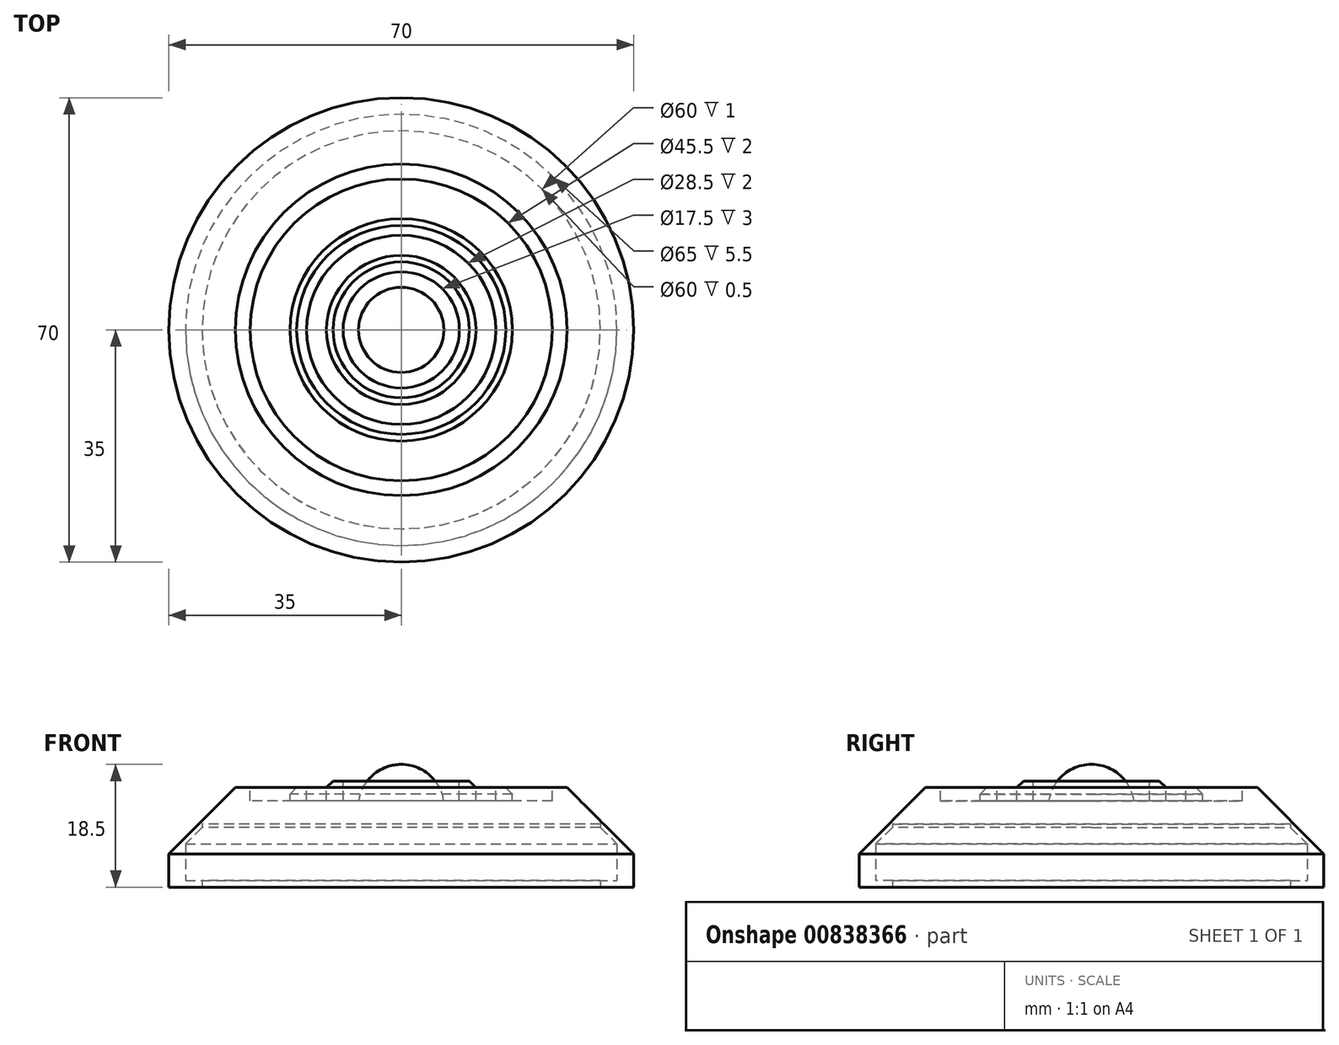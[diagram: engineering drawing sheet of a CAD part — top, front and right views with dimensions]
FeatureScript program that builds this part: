
annotation { "Feature Type Name" : "Feature", "Feature Type Description" : "" }
export const myFeature = defineFeature(function(context is Context, id is Id, definition is map)
    precondition{}
    {
        {
            var Q0;
            Q0=qCreatedBy(makeId("Top.planeOp"),FACE);
            var sketch = newSketch(context, id + "F0", { "sketchPlane" : qUnion([Q0])});
            skCircle(sketch, "E0", {"center": v(0, 0) * mm, "radius": 35 * mm});
            skSolve(sketch);
        }
        {
            var Q0;
            Q0 = qSketchRegion(id + "F0", true);
            extrude(context, id + "F1", {"entities" : qUnion([Q0]), "depth" : 15 * mm, "offsetDistance" : 25 * mm});
        }
        {
            var Q0;
            Q0=makeQuery(id+"F1.opExtrude","CAP_EDGE",EDGE,{"disambiguationData":[OSD([sQuery(id+"F0.wireOp",EDGE,"E0")])],"isStart":false});
            chamfer(context, id + "F2", {"entities" : qUnion([Q0]), "width" : 10 * mm, "tangentPropagation" : true});
        }
        {
            var Q0;
            Q0=qCreatedBy(makeId("Top.planeOp"),FACE);
            cPlane(context, id + "F3", {"entities" : qUnion([Q0]), "cplaneType" : CPlaneType.OFFSET, "offset" : 15 * mm, "width" : 150 * mm, "height" : 150 * mm});
        }
        {
            var Q0;
            Q0=qCreatedBy(id+"F3.planeOp",FACE);
            var sketch = newSketch(context, id + "F4", { "sketchPlane" : qUnion([Q0])});
            skCircle(sketch, "E1", {"center": v(0, 0) * mm, "radius": 22.75 * mm});
            skCircle(sketch, "E2.0", {"center": v(0, 0) * mm, "radius": 16.75 * mm});
            skCircle(sketch, "E3.0", {"center": v(0, 0) * mm, "radius": 14.25 * mm});
            skCircle(sketch, "E4.0", {"center": v(0, 0) * mm, "radius": 11.25 * mm});
            skCircle(sketch, "E5.0", {"center": v(0, 0) * mm, "radius": 8.75 * mm});
            skSolve(sketch);
        }
        {
            var Q0;
            Q0=makeQuery(id+"F4.imprint","IMPRINT",FACE,{"disambiguationData":[TD([[makeQuery(id+"F4.imprint","IMPRINT",EDGE,{"derivedFrom":sQuery(id+"F4.wireOp",EDGE,"E1")}),1.0]])]});
            extrude(context, id + "F5", {"entities" : qUnion([Q0]), "operationType" : NewBodyOperationType.REMOVE, "oppositeDirection" : true, "depth" : 2 * mm, "offsetDistance" : 25 * mm});
        }
        {
            var Q0;
            Q0=makeQuery(id+"F4.imprint","IMPRINT",FACE,{"disambiguationData":[TD([[makeQuery(id+"F4.imprint","IMPRINT",EDGE,{"derivedFrom":sQuery(id+"F4.wireOp",EDGE,"E3.0")}),1.0]])]});
            extrude(context, id + "F6", {"entities" : qUnion([Q0]), "operationType" : NewBodyOperationType.REMOVE, "oppositeDirection" : true, "depth" : 2 * mm, "offsetDistance" : 25 * mm});
        }
        {
            var Q0;
            Q0=makeQuery(id+"F4.imprint","IMPRINT",FACE,{"disambiguationData":[TD([[makeQuery(id+"F4.imprint","IMPRINT",EDGE,{"derivedFrom":sQuery(id+"F4.wireOp",EDGE,"E5.0")}),1.0]])]});
            extrude(context, id + "F7", {"entities" : qUnion([Q0]), "operationType" : NewBodyOperationType.REMOVE, "oppositeDirection" : true, "depth" : 2 * mm, "offsetDistance" : 25 * mm});
        }
        {
            var Q0;
            Q0=makeQuery(id+"F4.imprint","IMPRINT",FACE,{"disambiguationData":[TD([[makeQuery(id+"F4.imprint","IMPRINT",EDGE,{"derivedFrom":sQuery(id+"F4.wireOp",EDGE,"E4.0")}),1.0]])]});
            extrude(context, id + "F8", {"entities" : qUnion([Q0]), "operationType" : NewBodyOperationType.ADD, "depth" : 1 * mm, "offsetDistance" : 25 * mm});
        }
        {
            var Q0;
            Q0=qCreatedBy(makeId("Front.planeOp"),FACE);
            var sketch = newSketch(context, id + "F9", { "sketchPlane" : qUnion([Q0])});
            skLineSegment(sketch, "E6", {"start": v(0, 0) * mm, "end": v(0, 12) * mm});
            skCircle(sketch, "E7", {"center": v(0, 12) * mm, "radius": 6.5 * mm});
            skLineSegment(sketch, "E8", {"start": v(0, 12) * mm, "end": v(6.5, 12) * mm});
            skLineSegment(sketch, "E9", {"start": v(0, 12) * mm, "end": v(0, 18.5) * mm});
            skSolve(sketch);
        }
        {
            var Q0;
            {var subQ0=sQuery(id+"F9.wireOp",EDGE,"E8");Q0=makeQuery(id+"F9.imprint","IMPRINT",FACE,{"disambiguationData":[TD([[makeQuery(id+"F9.imprint","IMPRINT",EDGE,{"derivedFrom":subQ0}),-1.0]])]});}
            var Q1;
            {var subQ0=sQuery(id+"F9.wireOp",EDGE,"E8");Q1=makeQuery(id+"F9.imprint","IMPRINT",FACE,{"disambiguationData":[TD([[makeQuery(id+"F9.imprint","IMPRINT",EDGE,{"derivedFrom":subQ0}),1.0]])]});}
            var Q2;
            Q2=sQuery(id+"F9.wireOp",EDGE,"E6");
            revolve(context, id + "F10", {"operationType" : NewBodyOperationType.ADD, "surfaceOperationType" : NewSurfaceOperationType.NEW, "entities" : qUnion([Q0, Q1]), "axis" : qUnion([Q2]), "revolveType" : RevolveType.SYMMETRIC, "angle" : 360 * degree});
        }
        {
            var Q0;
            Q0=makeQuery(id+"F5.boolean.opBoolean","COPY",EDGE,{"derivedFrom":makeQuery(id+"F5.opExtrude","CAP_EDGE",EDGE,{"disambiguationData":[OSD([sQuery(id+"F4.wireOp",EDGE,"E1")])],"isStart":true})});
            var Q1;
            Q1=makeQuery(id+"F5.boolean.opBoolean","COPY",EDGE,{"derivedFrom":makeQuery(id+"F5.opExtrude","CAP_EDGE",EDGE,{"disambiguationData":[OSD([sQuery(id+"F4.wireOp",EDGE,"E2.0")])],"isStart":true})});
            var Q2;
            Q2=makeQuery(id+"F8.opExtrude","CAP_EDGE",EDGE,{"disambiguationData":[OSD([sQuery(id+"F4.wireOp",EDGE,"E4.0")])],"isStart":false});
            chamfer(context, id + "F11", {"entities" : qUnion([Q0, Q1, Q2]), "width" : 1 * mm, "tangentPropagation" : true});
        }
        {
            var Q0;
            Q0=qCreatedBy(makeId("Top.planeOp"),FACE);
            var sketch = newSketch(context, id + "F12", { "sketchPlane" : qUnion([Q0])});
            skCircle(sketch, "E10", {"center": v(0, 0) * mm, "radius": 30 * mm});
            skSolve(sketch);
        }
        {
            var Q0;
            Q0 = qSketchRegion(id + "F12", true);
            extrude(context, id + "F13", {"entities" : qUnion([Q0]), "operationType" : NewBodyOperationType.REMOVE, "depth" : 9.5 * mm, "offsetDistance" : 25 * mm});
        }
        {
            var Q0;
            Q0=qCreatedBy(makeId("Top.planeOp"),FACE);
            cPlane(context, id + "F14", {"entities" : qUnion([Q0]), "cplaneType" : CPlaneType.OFFSET, "offset" : 1 * mm, "width" : 150 * mm, "height" : 150 * mm});
        }
        {
            var Q0;
            Q0=qCreatedBy(id+"F14.planeOp",FACE);
            var sketch = newSketch(context, id + "F15", { "sketchPlane" : qUnion([Q0])});
            skCircle(sketch, "E11", {"center": v(0, 0) * mm, "radius": 32.5 * mm});
            skSolve(sketch);
        }
        {
            var Q0;
            Q0 = qSketchRegion(id + "F15", true);
            extrude(context, id + "F16", {"entities" : qUnion([Q0]), "operationType" : NewBodyOperationType.REMOVE, "depth" : 5 * mm, "offsetDistance" : 25 * mm});
        }
        {
            var Q0;
            Q0=makeQuery(id+"F16.boolean.opBoolean","INTERSECT",EDGE,{"derivedFrom":[makeQuery(id+"F13.boolean.opBoolean","COPY",FACE,{"derivedFrom":makeQuery(id+"F13.opExtrude","SWEPT_FACE",FACE,{"disambiguationData":[OSD([sQuery(id+"F12.wireOp",EDGE,"E10")])]})}),makeQuery(id+"F16.opExtrude","CAP_FACE",FACE,{"disambiguationData":[OSD([sQuery(id+"F15.wireOp",EDGE,"E11")])],"isStart":false})]});
            chamfer(context, id + "F17", {"entities" : qUnion([Q0]), "width" : 3 * mm, "tangentPropagation" : true});
        }
    });
